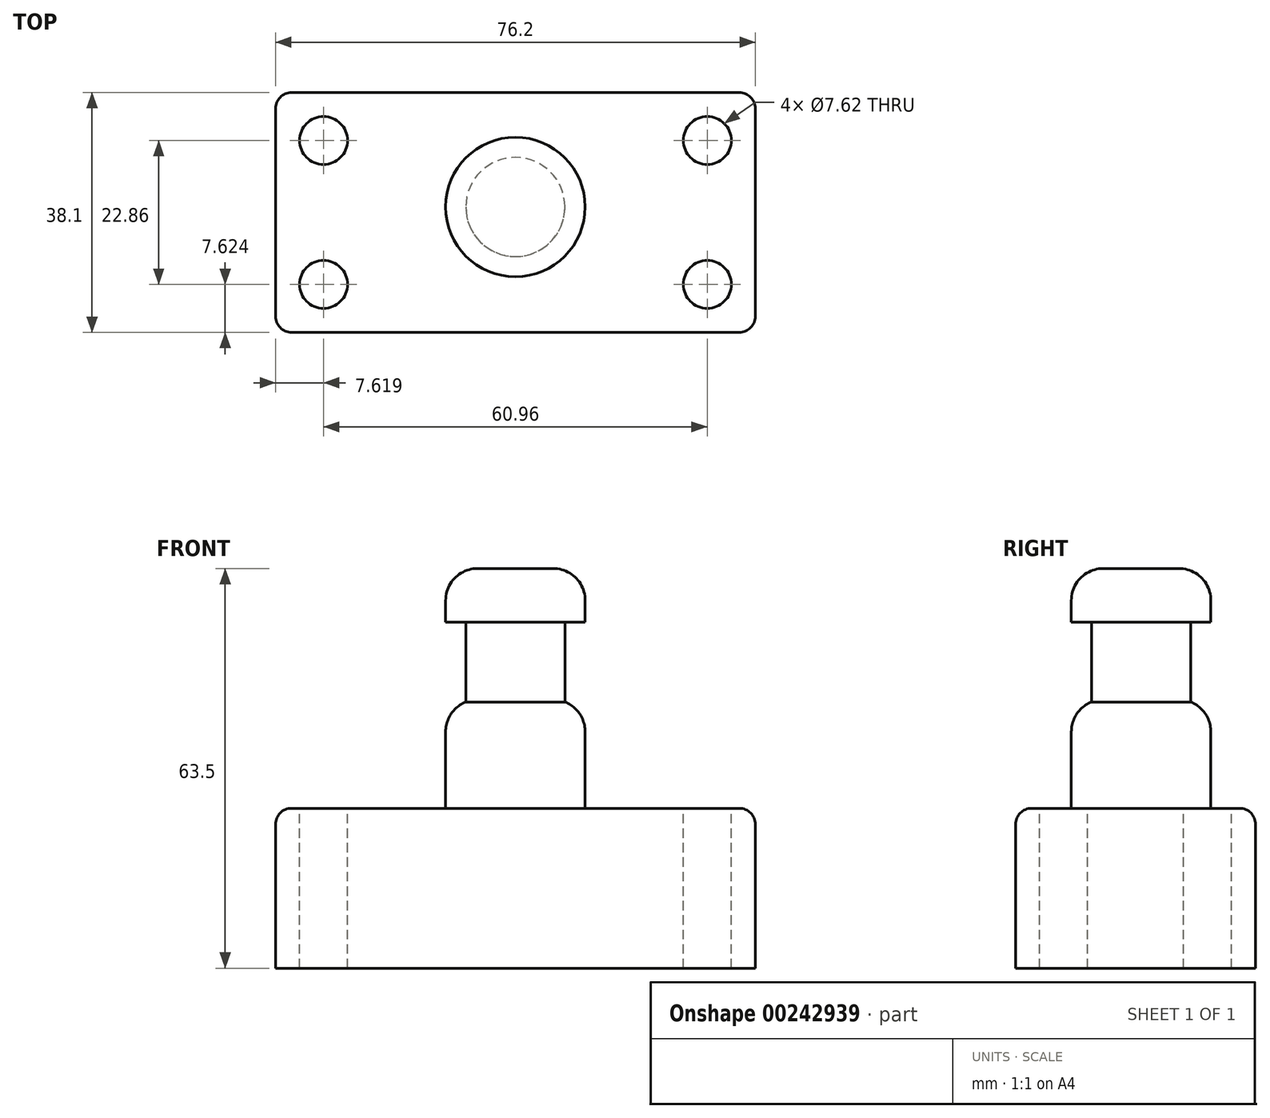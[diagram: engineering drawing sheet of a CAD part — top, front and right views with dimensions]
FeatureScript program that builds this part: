
annotation { "Feature Type Name" : "Feature", "Feature Type Description" : "" }
export const myFeature = defineFeature(function(context is Context, id is Id, definition is map)
    precondition{}
    {
        {
            var Q0;
            Q0=qCreatedBy(makeId("Top.planeOp"),FACE);
            var sketch = newSketch(context, id + "F0", { "sketchPlane" : qUnion([Q0])});
            skLineSegment(sketch, "E0.bottom", {"start": v(-35.67, 14.1) * mm, "end": v(40.53, 14.1) * mm});
            skLineSegment(sketch, "E0.top", {"start": v(-35.67, -24) * mm, "end": v(40.53, -24) * mm});
            skLineSegment(sketch, "E0.left", {"start": v(-35.67, 14.1) * mm, "end": v(-35.67, -24) * mm});
            skLineSegment(sketch, "E0.right", {"start": v(40.53, 14.1) * mm, "end": v(40.53, -24) * mm});
            skSolve(sketch);
        }
        {
            var Q0;
            Q0 = qSketchRegion(id + "F0", true);
            extrude(context, id + "F1", {"entities" : qUnion([Q0]), "depth" : 25.4 * mm});
        }
        {
            var Q0;
            Q0=makeQuery(id+"F1.opExtrude","CAP_FACE",FACE,{"disambiguationData":[OSD([sQuery(id+"F0.wireOp",EDGE,"E0.bottom"),sQuery(id+"F0.wireOp",EDGE,"E0.top"),sQuery(id+"F0.wireOp",EDGE,"E0.left"),sQuery(id+"F0.wireOp",EDGE,"E0.right")])],"isStart":false});
            var sketch = newSketch(context, id + "F2", { "sketchPlane" : qUnion([Q0])});
            skCircle(sketch, "E1", {"center": v(-28.05, 6.48) * mm, "radius": 3.81 * mm});
            skSolve(sketch);
        }
        {
            var Q0;
            Q0=makeQuery(id+"F1.opExtrude","CAP_FACE",FACE,{"disambiguationData":[OSD([sQuery(id+"F0.wireOp",EDGE,"E0.bottom"),sQuery(id+"F0.wireOp",EDGE,"E0.top"),sQuery(id+"F0.wireOp",EDGE,"E0.left"),sQuery(id+"F0.wireOp",EDGE,"E0.right")])],"isStart":false});
            var sketch = newSketch(context, id + "F3", { "sketchPlane" : qUnion([Q0])});
            skCircle(sketch, "E2", {"center": v(32.9, 6.48) * mm, "radius": 3.81 * mm});
            skSolve(sketch);
        }
        {
            var Q0;
            Q0=makeQuery(id+"F3.imprint","IMPRINT",FACE,{"disambiguationData":[TD([[makeQuery(id+"F3.imprint","IMPRINT",EDGE,{"derivedFrom":sQuery(id+"F3.wireOp",EDGE,"E2")}),1.0]])]});
            extrude(context, id + "F4", {"entities" : qUnion([Q0]), "operationType" : NewBodyOperationType.REMOVE, "oppositeDirection" : true, "depth" : 25.4 * mm});
        }
        {
            var Q0;
            Q0=makeQuery(id+"F2.imprint","IMPRINT",FACE,{"disambiguationData":[TD([[makeQuery(id+"F2.imprint","IMPRINT",EDGE,{"derivedFrom":sQuery(id+"F2.wireOp",EDGE,"E1")}),-1.0]])]});
            var sketch = newSketch(context, id + "F5", { "sketchPlane" : qUnion([Q0])});
            skCircle(sketch, "E3", {"center": v(2.43, -4.08) * mm, "radius": 11.08 * mm});
            skSolve(sketch);
        }
        {
            var Q0;
            Q0 = qSketchRegion(id + "F5", true);
            extrude(context, id + "F6", {"entities" : qUnion([Q0]), "operationType" : NewBodyOperationType.ADD, "depth" : 38.1 * mm});
        }
        {
            var Q0;
            Q0 = qSketchRegion(id + "F2", true);
            extrude(context, id + "F7", {"entities" : qUnion([Q0]), "operationType" : NewBodyOperationType.REMOVE, "oppositeDirection" : true, "depth" : 25.4 * mm});
        }
        {
            var Q0;
            Q0=makeQuery(id+"F1.opExtrude","CAP_FACE",FACE,{"disambiguationData":[OSD([sQuery(id+"F0.wireOp",EDGE,"E0.bottom"),sQuery(id+"F0.wireOp",EDGE,"E0.top"),sQuery(id+"F0.wireOp",EDGE,"E0.left"),sQuery(id+"F0.wireOp",EDGE,"E0.right")])],"isStart":false});
            var sketch = newSketch(context, id + "F8", { "sketchPlane" : qUnion([Q0])});
            skCircle(sketch, "E4", {"center": v(-28.05, -16.38) * mm, "radius": 3.81 * mm});
            skSolve(sketch);
        }
        {
            var Q0;
            Q0 = qSketchRegion(id + "F8", true);
            extrude(context, id + "F9", {"entities" : qUnion([Q0]), "operationType" : NewBodyOperationType.REMOVE, "oppositeDirection" : true, "depth" : 25.4 * mm});
        }
        {
            var Q0;
            Q0=qCreatedBy(makeId("Front.planeOp"),FACE);
            var sketch = newSketch(context, id + "F10", { "sketchPlane" : qUnion([Q0])});
            skLineSegment(sketch, "E5.bottom", {"start": v(-17, 54.98) * mm, "end": v(-4.3, 54.98) * mm});
            skLineSegment(sketch, "E5.top", {"start": v(-17, 42.28) * mm, "end": v(-4.3, 42.28) * mm});
            skLineSegment(sketch, "E5.left", {"start": v(-17, 54.98) * mm, "end": v(-17, 42.28) * mm});
            skLineSegment(sketch, "E5.right", {"start": v(-4.3, 54.98) * mm, "end": v(-4.3, 42.28) * mm});
            skSolve(sketch);
        }
        {
            var Q0;
            Q0=makeQuery(id+"F1.opExtrude","CAP_FACE",FACE,{"disambiguationData":[OSD([sQuery(id+"F0.wireOp",EDGE,"E0.bottom"),sQuery(id+"F0.wireOp",EDGE,"E0.top"),sQuery(id+"F0.wireOp",EDGE,"E0.left"),sQuery(id+"F0.wireOp",EDGE,"E0.right")])],"isStart":false});
            var sketch = newSketch(context, id + "F11", { "sketchPlane" : qUnion([Q0])});
            skCircle(sketch, "E6", {"center": v(32.9, -16.38) * mm, "radius": 3.81 * mm});
            skSolve(sketch);
        }
        {
            var Q0;
            Q0 = qSketchRegion(id + "F11", true);
            extrude(context, id + "F12", {"entities" : qUnion([Q0]), "operationType" : NewBodyOperationType.REMOVE, "oppositeDirection" : true, "depth" : 25.4 * mm});
        }
        {
            var Q0;
            Q0 = qSketchRegion(id + "F10", true);
            var Q1;
            Q1=makeQuery(id+"F6.opExtrude","SWEPT_FACE",FACE,{"disambiguationData":[OSD([sQuery(id+"F5.wireOp",EDGE,"E3")])]});
            revolve(context, id + "F13", {"operationType" : NewBodyOperationType.REMOVE, "entities" : qUnion([Q0]), "axis" : qUnion([Q1]), "revolveType" : RevolveType.FULL, "oppositeDirection" : true});
        }
        {
            var Q0;
            Q0=makeQuery(id+"F1.opExtrude","CAP_EDGE",EDGE,{"disambiguationData":[OSD([sQuery(id+"F0.wireOp",EDGE,"E0.top")])],"isStart":false});
            fillet(context, id + "F14", {"entities" : qUnion([Q0]), "radius" : 2.54 * mm, "tangentPropagation" : true, "allowEdgeOverflow" : false});
        }
        {
            var Q0;
            Q0=makeQuery(id+"F1.opExtrude","CAP_EDGE",EDGE,{"disambiguationData":[OSD([sQuery(id+"F0.wireOp",EDGE,"E0.left")])],"isStart":false});
            var Q1;
            Q1=makeQuery(id+"F1.opExtrude","CAP_EDGE",EDGE,{"disambiguationData":[OSD([sQuery(id+"F0.wireOp",EDGE,"E0.bottom")])],"isStart":false});
            var Q2;
            Q2=makeQuery(id+"F1.opExtrude","CAP_EDGE",EDGE,{"disambiguationData":[OSD([sQuery(id+"F0.wireOp",EDGE,"E0.right")])],"isStart":false});
            fillet(context, id + "F15", {"entities" : qUnion([Q0, Q1, Q2]), "radius" : 2.54 * mm, "tangentPropagation" : true, "allowEdgeOverflow" : false});
        }
        {
            var Q0;
            Q0=makeQuery(id+"F6.opExtrude","CAP_EDGE",EDGE,{"disambiguationData":[OSD([sQuery(id+"F5.wireOp",EDGE,"E3")])],"isStart":false});
            var Q1;
            Q1=makeQuery(id+"F13.boolean.opBoolean","INTERSECT",EDGE,{"derivedFrom":[makeQuery(id+"F6.opExtrude","SWEPT_FACE",FACE,{"disambiguationData":[OSD([sQuery(id+"F5.wireOp",EDGE,"E3")])]}),makeQuery(id+"F13.opRevolve","SWEPT_FACE",FACE,{"disambiguationData":[OSD([sQuery(id+"F10.wireOp",EDGE,"E5.top")])]})]});
            fillet(context, id + "F16", {"entities" : qUnion([Q0, Q1]), "radius" : 5.08 * mm, "tangentPropagation" : true, "allowEdgeOverflow" : false});
        }
        {
            var Q0;
            Q0=makeQuery(id+"F1.opExtrude","SWEPT_EDGE",EDGE,{"disambiguationData":[OSD([sQuery(id+"F0.wireOp",EDGE,"E0.bottom"),sQuery(id+"F0.wireOp",EDGE,"E0.left")])]});
            var Q1;
            Q1=makeQuery(id+"F1.opExtrude","SWEPT_EDGE",EDGE,{"disambiguationData":[OSD([sQuery(id+"F0.wireOp",EDGE,"E0.bottom"),sQuery(id+"F0.wireOp",EDGE,"E0.right")])]});
            fillet(context, id + "F17", {"entities" : qUnion([Q0, Q1]), "radius" : 2.54 * mm, "tangentPropagation" : true, "allowEdgeOverflow" : false});
        }
    });
